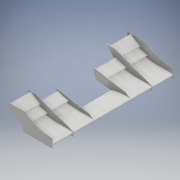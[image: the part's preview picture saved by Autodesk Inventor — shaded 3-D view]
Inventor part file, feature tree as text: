
AUTODESK INVENTOR PART (.ipt)
format: ipt  version: 2018.2 (Build 222227000, 227)  size: 710,656 bytes
history: native  units: mm
features: projected_geometry x11, extrude x9, sketch x9, mirror x2, other x1
ambient origin geometry x8: Origin, YZ Plane, XZ Plane, XY Plane, X Axis, Y Axis, Z Axis, Center Point
bodies: Body1 (feature_tree)
feature tree (32):
  extrude  "押し出し7"  Depth=394.0mm TaperAngle=0.0deg
  extrude  "押し出し8"  Depth=5.0mm TaperAngle=0.0deg
  extrude  "押し出し9"  Depth=225.0mm TaperAngle=0.0deg
  extrude  "押し出し10"  Depth=5.0mm TaperAngle=0.0deg
  extrude  "押し出し11"  Depth=225.0mm TaperAngle=0.0deg
  extrude  "押し出し12"  Depth=2.0mm TaperAngle=0.0deg
  extrude  "押し出し13"  Depth=2.0mm
  extrude  "押し出し14"  Depth=5.0mm
  mirror  "ミラー2"
  extrude  "押し出し15"  Depth=225.0mm TaperAngle=0.0deg
  mirror  "ミラー3"
  other  "ソリッド36"
  sketch  "スケッチ8"
  projected_geometry  "投影ループ7"
  sketch  "スケッチ9"
  projected_geometry  "投影ループ8"
  sketch  "スケッチ10"
  projected_geometry  "投影ループ9"
  projected_geometry  "投影ループ10"
  sketch  "スケッチ11"
  projected_geometry  "投影ループ11"
  sketch  "スケッチ12"
  projected_geometry  "投影ループ12"
  projected_geometry  "投影ループ13"
  projected_geometry  "投影ループ14"
  sketch  "スケッチ13"
  projected_geometry  "投影ループ15"
  sketch  "スケッチ14"
  projected_geometry  "投影ループ16"
  sketch  "スケッチ15"
  projected_geometry  "投影ループ17"
  sketch  "スケッチ16"
